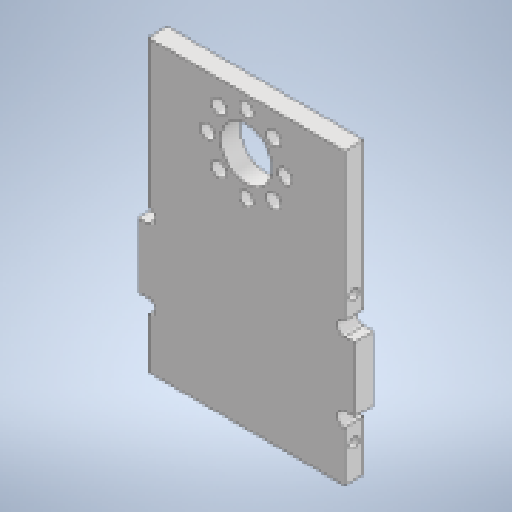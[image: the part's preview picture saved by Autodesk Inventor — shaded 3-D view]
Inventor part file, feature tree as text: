
AUTODESK INVENTOR PART (.ipt)
format: ipt  version: 2025.1 (Build 291241000, 241)  size: 285,184 bytes
history: native  units: mm
features: extrude x4, sketch x4, other x2, hole x1
ambient origin geometry x8: Origin, YZ Plane, XZ Plane, XY Plane, X Axis, Y Axis, Z Axis, Center Point
bodies: Body1 (feature_tree)
feature tree (11):
  other  "ソリッド1"
  extrude  "押し出し1"  Depth=30.5mm
  sketch  "スケッチ2"
  extrude  "押し出し2"  Depth=45.0mm
  extrude  "押し出し3"  Depth=3.0mm TaperAngle=0.0deg
  hole  "穴1"  [1 undecoded]
  extrude  "押し出し4"  Depth=1.5mm
  sketch  "スケッチ1"
  sketch  "スケッチ3"
  sketch  "スケッチ4"
  other  "スケッチ円形状パターン1"
note: 1 required parameter value undecoded (feature->parameter linkage not recoverable at this tier; creation-order binding heuristic only, values carry confidence <= 0.55)
